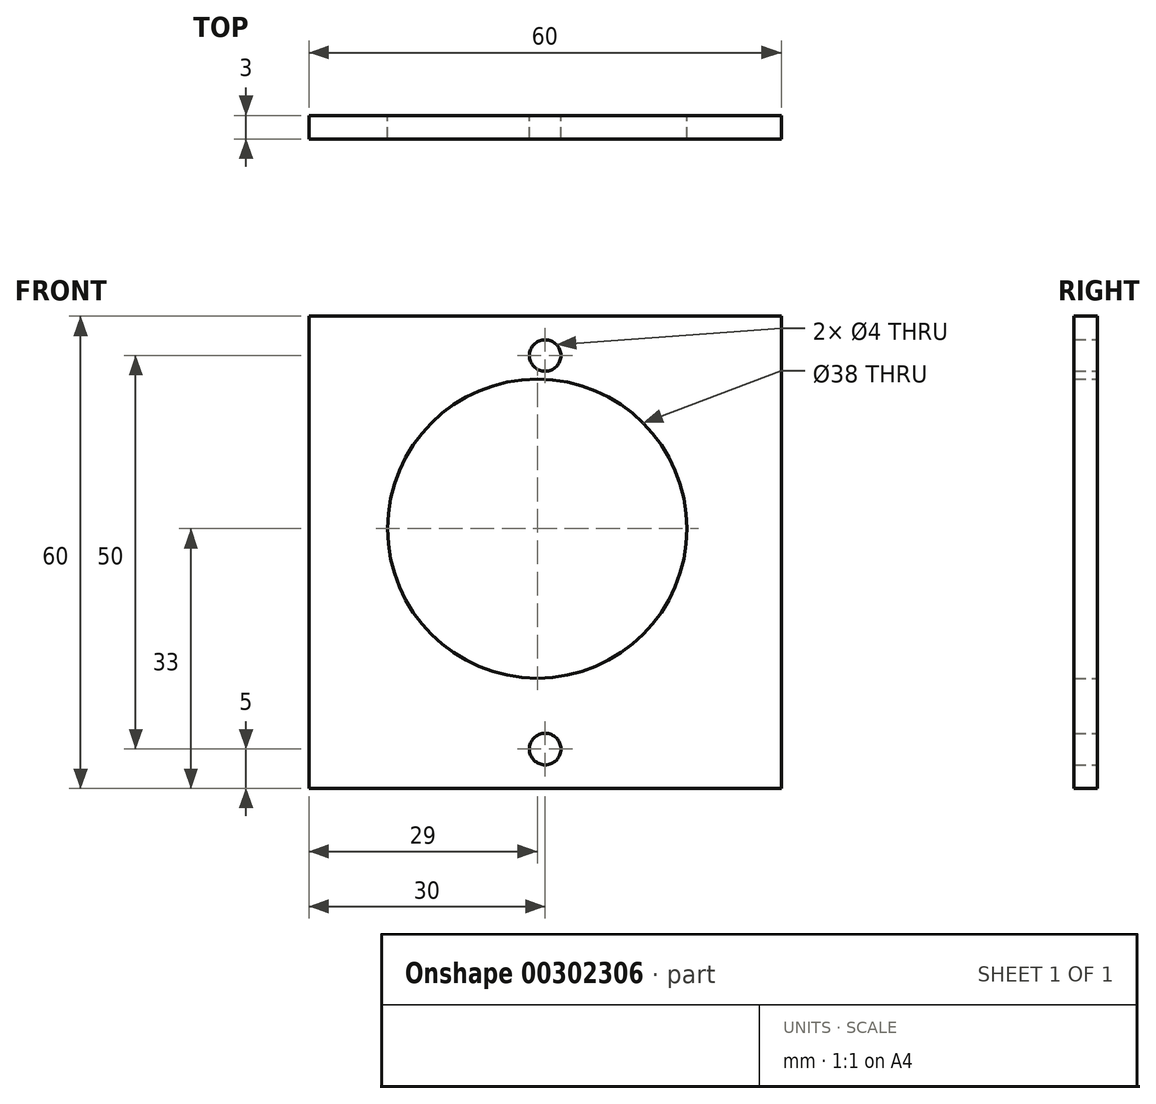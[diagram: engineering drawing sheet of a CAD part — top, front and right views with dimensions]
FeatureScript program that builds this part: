
annotation { "Feature Type Name" : "Feature", "Feature Type Description" : "" }
export const myFeature = defineFeature(function(context is Context, id is Id, definition is map)
    precondition{}
    {
        {
            var Q0;
            Q0=qCreatedBy(makeId("Front.planeOp"),FACE);
            var sketch = newSketch(context, id + "F0", { "sketchPlane" : qUnion([Q0])});
            skLineSegment(sketch, "E0.bottom", {"start": v(-30, 30) * mm, "end": v(30, 30) * mm});
            skLineSegment(sketch, "E0.top", {"start": v(-30, -30) * mm, "end": v(30, -30) * mm});
            skLineSegment(sketch, "E0.left", {"start": v(-30, 30) * mm, "end": v(-30, -30) * mm});
            skLineSegment(sketch, "E0.right", {"start": v(30, 30) * mm, "end": v(30, -30) * mm});
            skPoint(sketch, "E0.middle", {"position": v(0, 0) * mm});
            skCircle(sketch, "E1", {"center": v(-1, 3) * mm, "radius": 19 * mm});
            skCircle(sketch, "E2", {"center": v(0, 25) * mm, "radius": 2 * mm});
            skCircle(sketch, "E3", {"center": v(0, -25) * mm, "radius": 2 * mm});
            skSolve(sketch);
        }
        {
            var Q0;
            Q0=makeQuery(id+"F0.imprint","IMPRINT",FACE,{"disambiguationData":[TD([[makeQuery(id+"F0.imprint","IMPRINT",EDGE,{"derivedFrom":sQuery(id+"F0.wireOp",EDGE,"E0.bottom")}),-1.0]])]});
            extrude(context, id + "F1", {"entities" : qUnion([Q0]), "depth" : 3 * mm});
        }
    });
